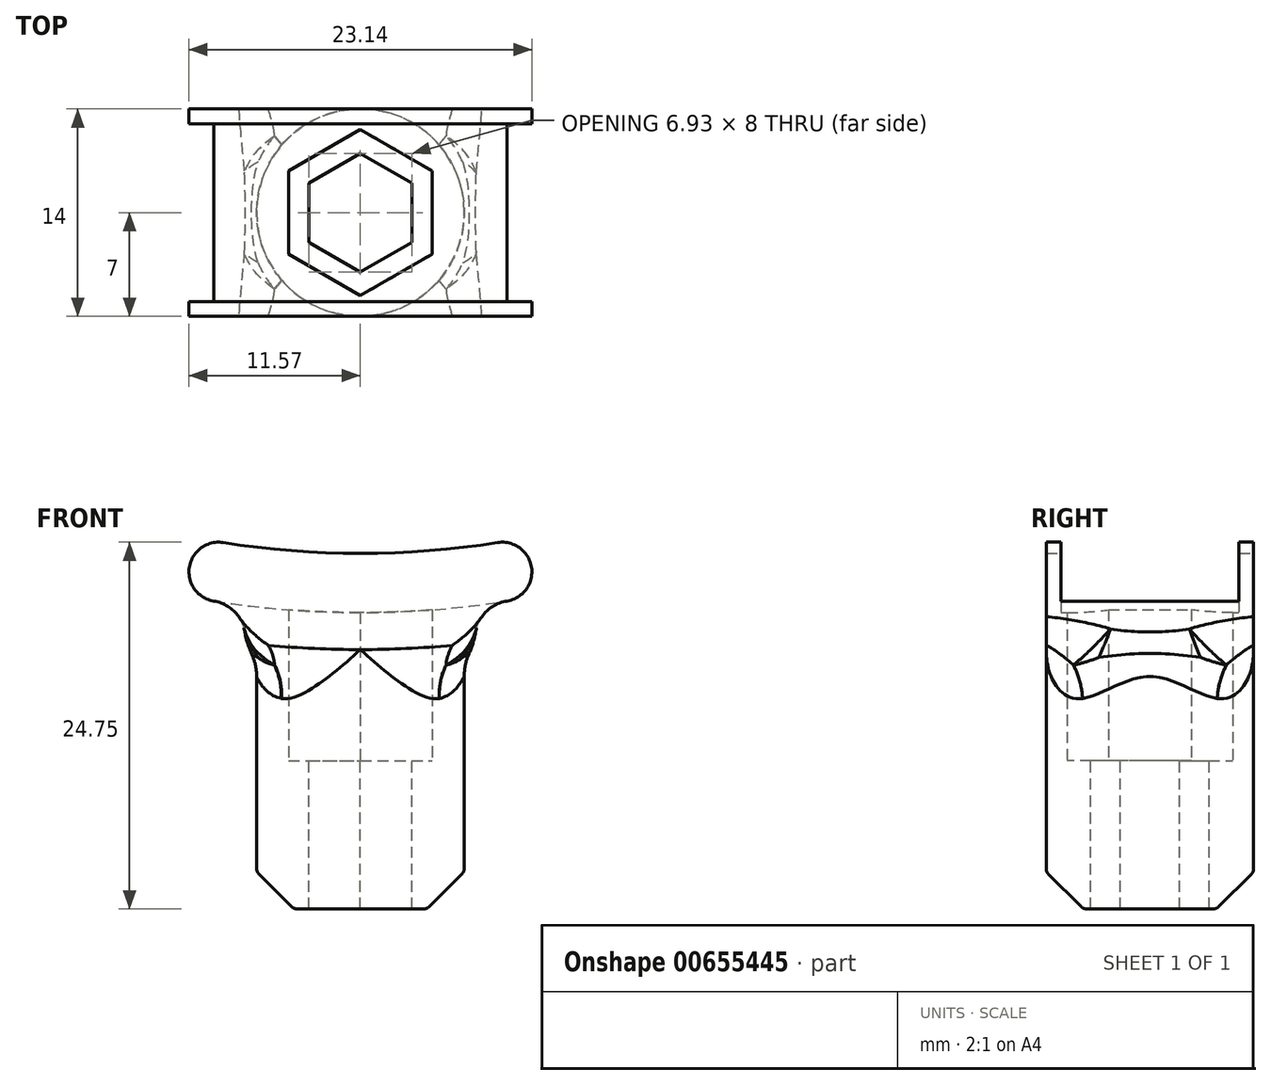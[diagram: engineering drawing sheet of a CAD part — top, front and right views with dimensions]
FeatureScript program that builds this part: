
annotation { "Feature Type Name" : "Feature", "Feature Type Description" : "" }
export const myFeature = defineFeature(function(context is Context, id is Id, definition is map)
    precondition{}
    {
        {
            var Q0;
            Q0=qCreatedBy(makeId("Top.planeOp"),FACE);
            var sketch = newSketch(context, id + "F0", { "sketchPlane" : qUnion([Q0])});
            skCircle(sketch, "E0.cCircle", {"center": v(0, 0) * mm, "radius": 5.6 * mm, "construction": true});
            skLineSegment(sketch, "E0.0", {"start": v(0, 5.6) * mm, "end": v(4.85, 2.8) * mm});
            skLineSegment(sketch, "E0.1", {"start": v(4.85, 2.8) * mm, "end": v(4.85, -2.8) * mm});
            skLineSegment(sketch, "E0.2", {"start": v(4.85, -2.8) * mm, "end": v(0, -5.6) * mm});
            skLineSegment(sketch, "E0.3", {"start": v(0, -5.6) * mm, "end": v(-4.85, -2.8) * mm});
            skLineSegment(sketch, "E0.4", {"start": v(-4.85, -2.8) * mm, "end": v(-4.85, 2.8) * mm});
            skLineSegment(sketch, "E0.5", {"start": v(-4.85, 2.8) * mm, "end": v(0, 5.6) * mm});
            skCircle(sketch, "E1.cCircle", {"center": v(0, 0) * mm, "radius": 4 * mm, "construction": true});
            skLineSegment(sketch, "E1.0", {"start": v(0, 4) * mm, "end": v(3.46, 2) * mm});
            skLineSegment(sketch, "E1.1", {"start": v(3.46, 2) * mm, "end": v(3.46, -2) * mm});
            skLineSegment(sketch, "E1.2", {"start": v(3.46, -2) * mm, "end": v(0, -4) * mm});
            skLineSegment(sketch, "E1.3", {"start": v(0, -4) * mm, "end": v(-3.46, -2) * mm});
            skLineSegment(sketch, "E1.4", {"start": v(-3.46, -2) * mm, "end": v(-3.46, 2) * mm});
            skLineSegment(sketch, "E1.5", {"start": v(-3.46, 2) * mm, "end": v(0, 4) * mm});
            skCircle(sketch, "E2", {"center": v(0, 0) * mm, "radius": 7 * mm});
            skSolve(sketch);
        }
        {
            var Q0;
            Q0=makeQuery(id+"F0.imprint","IMPRINT",FACE,{"disambiguationData":[TD([[makeQuery(id+"F0.imprint","IMPRINT",EDGE,{"derivedFrom":sQuery(id+"F0.wireOp",EDGE,"E0.0")}),1.0]])]});
            extrude(context, id + "F1", {"entities" : qUnion([Q0]), "depth" : 10 * mm, "offsetDistance" : 25 * mm});
        }
        {
            var Q0;
            Q0=makeQuery(id+"F0.imprint","IMPRINT",FACE,{"disambiguationData":[TD([[makeQuery(id+"F0.imprint","IMPRINT",EDGE,{"derivedFrom":sQuery(id+"F0.wireOp",EDGE,"E0.0")}),-1.0]])]});
            var Q1;
            Q1=makeQuery(id+"F0.imprint","IMPRINT",FACE,{"disambiguationData":[TD([[makeQuery(id+"F0.imprint","IMPRINT",EDGE,{"derivedFrom":sQuery(id+"F0.wireOp",EDGE,"E0.0")}),1.0]])]});
            extrude(context, id + "F2", {"entities" : qUnion([Q0, Q1]), "operationType" : NewBodyOperationType.ADD, "oppositeDirection" : true, "depth" : 10 * mm, "offsetDistance" : 25 * mm});
        }
        {
            var Q0;
            Q0=makeQuery(id+"F2.opExtrude","CAP_EDGE",EDGE,{"disambiguationData":[OSD([sQuery(id+"F0.wireOp",EDGE,"E2")])],"isStart":false});
            chamfer(context, id + "F3", {"entities" : qUnion([Q0]), "width" : 2.5 * mm, "tangentPropagation" : true});
        }
        {
            var Q0;
            {var subQ0=sQuery(id+"F0.wireOp",EDGE,"E2");Q0=makeQuery(id+"F3.opChamfer","BLEND_EDGE",EDGE,{"blendedFrom":[makeQuery(id+"F2.opExtrude","CAP_EDGE",EDGE,{"disambiguationData":[OSD([subQ0])],"isStart":false}),makeQuery(id+"F2.opExtrude","CAP_FACE",FACE,{"disambiguationData":[OSD([sQuery(id+"F0.wireOp",EDGE,"E1.0"),sQuery(id+"F0.wireOp",EDGE,"E1.1"),sQuery(id+"F0.wireOp",EDGE,"E1.2"),sQuery(id+"F0.wireOp",EDGE,"E1.3"),sQuery(id+"F0.wireOp",EDGE,"E1.4"),sQuery(id+"F0.wireOp",EDGE,"E1.5"),subQ0])],"isStart":false})],"blendedInto":[makeQuery(id+"F2.opExtrude","CAP_FACE",FACE,{"disambiguationData":[OSD([sQuery(id+"F0.wireOp",EDGE,"E1.0"),sQuery(id+"F0.wireOp",EDGE,"E1.1"),sQuery(id+"F0.wireOp",EDGE,"E1.2"),sQuery(id+"F0.wireOp",EDGE,"E1.3"),sQuery(id+"F0.wireOp",EDGE,"E1.4"),sQuery(id+"F0.wireOp",EDGE,"E1.5"),subQ0])],"isStart":false})]});}
            var Q1;
            {var subQ0=sQuery(id+"F0.wireOp",EDGE,"E2");Q1=makeQuery(id+"F3.opChamfer","BLEND_EDGE",EDGE,{"blendedFrom":[makeQuery(id+"F2.opExtrude","CAP_EDGE",EDGE,{"disambiguationData":[OSD([subQ0])],"isStart":false}),makeQuery(id+"F2.boolean.opBoolean","MERGE",FACE,{"derivedFrom":[makeQuery(id+"F1.opExtrude","SWEPT_FACE",FACE,{"disambiguationData":[OSD([subQ0])]}),makeQuery(id+"F2.opExtrude","SWEPT_FACE",FACE,{"disambiguationData":[OSD([subQ0])]})]})],"blendedInto":[makeQuery(id+"F2.boolean.opBoolean","MERGE",FACE,{"derivedFrom":[makeQuery(id+"F1.opExtrude","SWEPT_FACE",FACE,{"disambiguationData":[OSD([subQ0])]}),makeQuery(id+"F2.opExtrude","SWEPT_FACE",FACE,{"disambiguationData":[OSD([subQ0])]})]})]});}
            fillet(context, id + "F4", {"entities" : qUnion([Q0, Q1]), "radius" : .5 * mm, "tangentPropagation" : true, "allowEdgeOverflow" : false});
        }
        {
            var Q0;
            Q0=qCreatedBy(makeId("Front.planeOp"),FACE);
            var sketch = newSketch(context, id + "F5", { "sketchPlane" : qUnion([Q0])});
            skLineSegment(sketch, "E3", {"start": v(0, 0) * mm, "end": v(0, 73.5) * mm, "construction": true});
            skLineSegment(sketch, "E4", {"start": v(0, 0) * mm, "end": v(0, 10) * mm, "construction": true});
            skLineSegment(sketch, "E5", {"start": v(0, 10) * mm, "end": v(10, 10) * mm, "construction": true});
            skArc(sketch, "E6", {"start": v(0, 10) * mm, "mid": v(4.95, 10.2) * mm, "end": v(9.88, 10.77) * mm});
            skArc(sketch, "E7.MirrorCS", {"start": v(0, 10) * mm, "mid": v(-4.95, 10.2) * mm, "end": v(-9.88, 10.77) * mm});
            skArc(sketch, "E8.0", {"start": v(0, 14) * mm, "mid": v(4.64, 14.18) * mm, "end": v(9.26, 14.72) * mm});
            skArc(sketch, "E8.1", {"start": v(0, 14) * mm, "mid": v(-4.64, 14.18) * mm, "end": v(-9.26, 14.72) * mm});
            skArc(sketch, "E9.0", {"start": v(0, 7.5) * mm, "mid": v(-5.15, 7.7) * mm, "end": v(-10.27, 8.3) * mm});
            skArc(sketch, "E9.1", {"start": v(0, 7.5) * mm, "mid": v(5.15, 7.7) * mm, "end": v(10.27, 8.3) * mm});
            skArc(sketch, "E10", {"start": v(-9.88, 10.77) * mm, "mid": v(-11.54, 13.06) * mm, "end": v(-9.26, 14.72) * mm});
            skArc(sketch, "E11", {"start": v(9.88, 10.77) * mm, "mid": v(11.54, 13.06) * mm, "end": v(9.26, 14.72) * mm});
            skArc(sketch, "E12", {"start": v(-9.88, 10.77) * mm, "mid": v(-8.26, 9.8) * mm, "end": v(-7.8, 7.96) * mm});
            skArc(sketch, "E13", {"start": v(9.88, 10.77) * mm, "mid": v(8.25, 9.8) * mm, "end": v(7.76, 7.96) * mm});
            skSolve(sketch);
        }
        {
            var Q0;
            Q0=makeQuery(id+"F5.imprint","IMPRINT",FACE,{"disambiguationData":[TD([[makeQuery(id+"F5.imprint","IMPRINT",EDGE,{"derivedFrom":sQuery(id+"F5.wireOp",EDGE,"E6")}),-1.0]])]});
            var Q1;
            Q1=makeQuery(id+"F5.imprint","IMPRINT",FACE,{"disambiguationData":[TD([[makeQuery(id+"F5.imprint","IMPRINT",EDGE,{"derivedFrom":sQuery(id+"F5.wireOp",EDGE,"E6")}),1.0]])]});
            extrude(context, id + "F6", {"entities" : qUnion([Q0, Q1]), "operationType" : NewBodyOperationType.ADD, "endBound" : BoundingType.SYMMETRIC, "depth" : 14 * mm, "offsetDistance" : 25 * mm});
        }
        {
            var Q0;
            Q0=makeQuery(id+"F5.imprint","IMPRINT",FACE,{"disambiguationData":[TD([[makeQuery(id+"F5.imprint","IMPRINT",EDGE,{"derivedFrom":sQuery(id+"F5.wireOp",EDGE,"E6")}),1.0]])]});
            extrude(context, id + "F7", {"entities" : qUnion([Q0]), "operationType" : NewBodyOperationType.REMOVE, "endBound" : BoundingType.SYMMETRIC, "depth" : 12 * mm, "offsetDistance" : 25 * mm});
        }
        {
            var Q0;
            {var subQ0=sQuery(id+"F0.wireOp",EDGE,"E2");Q0=makeQuery(id+"F6.boolean.opBoolean","INTERSECT",EDGE,{"disambiguationData":[OD(1.0)],"derivedFrom":[makeQuery(id+"F2.boolean.opBoolean","MERGE",FACE,{"derivedFrom":[makeQuery(id+"F1.opExtrude","SWEPT_FACE",FACE,{"disambiguationData":[OSD([subQ0])]}),makeQuery(id+"F2.opExtrude","SWEPT_FACE",FACE,{"disambiguationData":[OSD([subQ0])]})]}),makeQuery(id+"F6.opExtrude","SWEPT_FACE",FACE,{"disambiguationData":[OSD([sQuery(id+"F5.wireOp",EDGE,"E9.0"),sQuery(id+"F5.wireOp",EDGE,"E9.1")])]})]});}
            var Q1;
            {var subQ0=sQuery(id+"F0.wireOp",EDGE,"E2");Q1=makeQuery(id+"F6.boolean.opBoolean","INTERSECT",EDGE,{"disambiguationData":[OD(0.0)],"derivedFrom":[makeQuery(id+"F2.boolean.opBoolean","MERGE",FACE,{"derivedFrom":[makeQuery(id+"F1.opExtrude","SWEPT_FACE",FACE,{"disambiguationData":[OSD([subQ0])]}),makeQuery(id+"F2.opExtrude","SWEPT_FACE",FACE,{"disambiguationData":[OSD([subQ0])]})]}),makeQuery(id+"F6.opExtrude","SWEPT_FACE",FACE,{"disambiguationData":[OSD([sQuery(id+"F5.wireOp",EDGE,"E9.0"),sQuery(id+"F5.wireOp",EDGE,"E9.1")])]})]});}
            fillet(context, id + "F8", {"entities" : qUnion([Q0, Q1]), "radius" : 3.78 * mm, "tangentPropagation" : true, "allowEdgeOverflow" : false});
        }
        {
            var Q0;
            {var subQ0=sQuery(id+"F0.wireOp",EDGE,"E2");Q0=makeQuery(id+"F8.opFillet","BLEND_EDGE",EDGE,{"blendedFrom":[makeQuery(id+"F6.boolean.opBoolean","INTERSECT",EDGE,{"disambiguationData":[OD(0.0)],"derivedFrom":[makeQuery(id+"F2.boolean.opBoolean","MERGE",FACE,{"derivedFrom":[makeQuery(id+"F1.opExtrude","SWEPT_FACE",FACE,{"disambiguationData":[OSD([subQ0])]}),makeQuery(id+"F2.opExtrude","SWEPT_FACE",FACE,{"disambiguationData":[OSD([subQ0])]})]}),makeQuery(id+"F6.opExtrude","SWEPT_FACE",FACE,{"disambiguationData":[OSD([sQuery(id+"F5.wireOp",EDGE,"E9.0"),sQuery(id+"F5.wireOp",EDGE,"E9.1")])]})]}),makeQuery(id+"F6.opExtrude","SWEPT_FACE",FACE,{"disambiguationData":[OSD([sQuery(id+"F5.wireOp",EDGE,"E12")])]})],"blendedInto":[makeQuery(id+"F6.opExtrude","SWEPT_FACE",FACE,{"disambiguationData":[OSD([sQuery(id+"F5.wireOp",EDGE,"E12")])]})]});}
            var Q1;
            {var subQ0=sQuery(id+"F0.wireOp",EDGE,"E2");Q1=makeQuery(id+"F8.opFillet","BLEND_EDGE",EDGE,{"blendedFrom":[makeQuery(id+"F6.boolean.opBoolean","INTERSECT",EDGE,{"disambiguationData":[OD(1.0)],"derivedFrom":[makeQuery(id+"F2.boolean.opBoolean","MERGE",FACE,{"derivedFrom":[makeQuery(id+"F1.opExtrude","SWEPT_FACE",FACE,{"disambiguationData":[OSD([subQ0])]}),makeQuery(id+"F2.opExtrude","SWEPT_FACE",FACE,{"disambiguationData":[OSD([subQ0])]})]}),makeQuery(id+"F6.opExtrude","SWEPT_FACE",FACE,{"disambiguationData":[OSD([sQuery(id+"F5.wireOp",EDGE,"E9.0"),sQuery(id+"F5.wireOp",EDGE,"E9.1")])]})]}),makeQuery(id+"F6.opExtrude","SWEPT_FACE",FACE,{"disambiguationData":[OSD([sQuery(id+"F5.wireOp",EDGE,"E13")])]})],"blendedInto":[makeQuery(id+"F6.opExtrude","SWEPT_FACE",FACE,{"disambiguationData":[OSD([sQuery(id+"F5.wireOp",EDGE,"E13")])]})]});}
            fillet(context, id + "F9", {"entities" : qUnion([Q0, Q1]), "radius" : 5.9 * mm, "allowEdgeOverflow" : false});
        }
        {
            var Q0;
            Q0=makeQuery(id+"F0.imprint","IMPRINT",FACE,{"disambiguationData":[TD([[makeQuery(id+"F0.imprint","IMPRINT",EDGE,{"derivedFrom":sQuery(id+"F0.wireOp",EDGE,"E0.0")}),-1.0]])]});
            var Q1;
            Q1=makeQuery(id+"F0.imprint","IMPRINT",FACE,{"disambiguationData":[TD([[makeQuery(id+"F0.imprint","IMPRINT",EDGE,{"derivedFrom":sQuery(id+"F0.wireOp",EDGE,"E1.0")}),-1.0]])]});
            extrude(context, id + "F10", {"entities" : qUnion([Q0, Q1]), "operationType" : NewBodyOperationType.REMOVE, "depth" : 10.2 * mm, "offsetDistance" : 25 * mm});
        }
    });
